# Revit family: QF_MACOM_FHP-47B
name_source: partatom
category: Equipamento especial
units: mm (PartAtom-declared; Revit-internal decimal feet)

## family parameters
Com base no plano de trabalho = Não
Compartilhado = Não
Corte com vazios quando carregada = Não
Cota do conector redondo = Utilizar diâmetro
Número OmniClass = 23.40.40.11.11.14
Ponto de cálculo do ambiente = Não
Sempre na vertical = Sim
Tipo de parte = Normal
Título OmniClass = Freezers

## types (1)
- FHP-47B
    Capacity in Liters = 90.0 L
    Cycle = 60 Hz
    Depth = 703 mm
    Descrição = FREEZEER HORIZONTAL PORTÁTIL MACOM
    Elec Connection Height = 153 mm
    Electric Power = 313 W
    Elevação padrão = 0 mm
    Fabricante = MACOM
    Height = 901 mm
    Ingress Protection Code = IP 22
    Modelo = FHP-47B
    Operational Current = 2 A
    Refrigerant Type = R134a
    Refrigeration Climate Class = 5
    URL = https://www.acosmacom.com.br
    Volts = 220 V
    Volume = 0.29 m³
    Weight = 88.00 kg
    Width = 445 mm
    Work Temperature = -20ºC a -10ºC

## geometry (parser evidence)
native form markers: Sweep x6
no freeform markers — native parametric forms only
